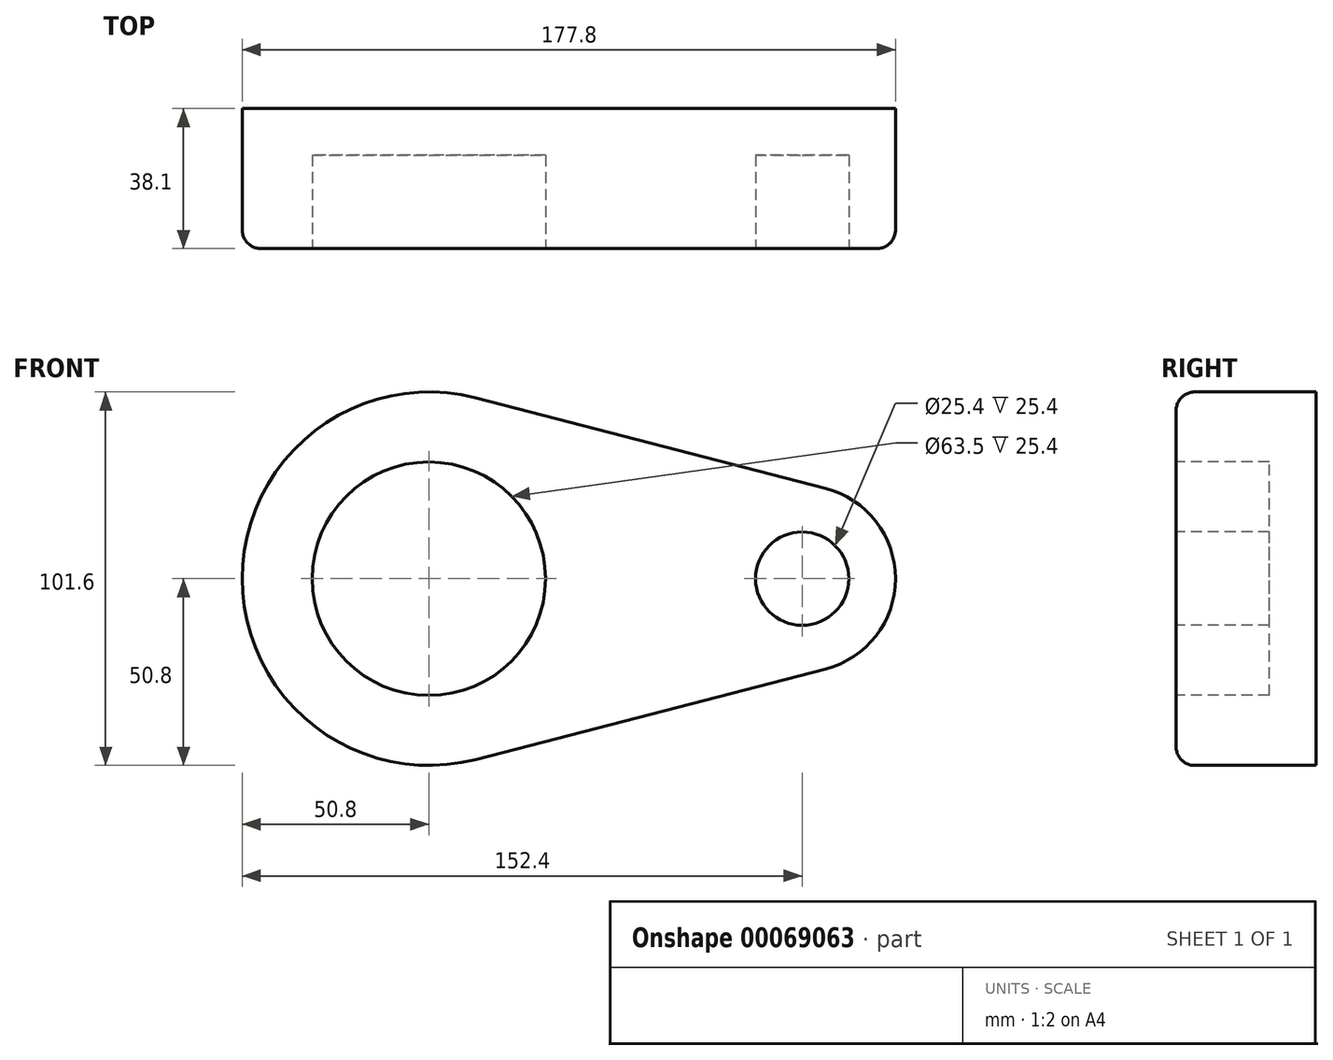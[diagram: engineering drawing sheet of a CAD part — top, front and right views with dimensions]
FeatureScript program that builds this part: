
annotation { "Feature Type Name" : "Feature", "Feature Type Description" : "" }
export const myFeature = defineFeature(function(context is Context, id is Id, definition is map)
    precondition{}
    {
        {
            var Q0;
            Q0=qCreatedBy(makeId("Front.planeOp"),FACE);
            var sketch = newSketch(context, id + "F3", { "sketchPlane" : qUnion([Q0])});
            skCircle(sketch, "E0", {"center": v(0, 0) * mm, "radius": 50.8 * mm});
            skCircle(sketch, "E1", {"center": v(101.6, 0) * mm, "radius": 25.4 * mm});
            skLineSegment(sketch, "E2", {"start": v(12.7, 49.19) * mm, "end": v(107.95, 24.6) * mm});
            skLineSegment(sketch, "E3", {"start": v(12.7, -49.19) * mm, "end": v(107.95, -24.6) * mm});
            skSolve(sketch);
        }
        {
            var Q0;
            {var subQ0=sQuery(id+"F3.wireOp",EDGE,"E2");Q0=makeQuery(id+"F3.imprint","IMPRINT",FACE,{"disambiguationData":[TD([[makeQuery(id+"F3.imprint","IMPRINT",EDGE,{"derivedFrom":subQ0}),-1.0]])]});}
            var Q1;
            {var subQ0=sQuery(id+"F3.wireOp",EDGE,"E0");var subQ1=makeQuery(id+"F3.imprint","INTERSECT",VERTEX,{"derivedFrom":[subQ0,sQuery(id+"F3.wireOp",EDGE,"E2")]});Q1=makeQuery(id+"F3.imprint","IMPRINT",FACE,{"disambiguationData":[TD([[makeQuery(id+"F3.imprint","IMPRINT",EDGE,{"disambiguationData":[TD([[subQ1,-1.0]])],"derivedFrom":subQ0}),1.0]])]});}
            var Q2;
            {var subQ0=sQuery(id+"F3.wireOp",EDGE,"E1");var subQ1=makeQuery(id+"F3.imprint","INTERSECT",VERTEX,{"derivedFrom":[subQ0,sQuery(id+"F3.wireOp",EDGE,"E2")]});Q2=makeQuery(id+"F3.imprint","IMPRINT",FACE,{"disambiguationData":[TD([[makeQuery(id+"F3.imprint","IMPRINT",EDGE,{"disambiguationData":[TD([[subQ1,-1.0]])],"derivedFrom":subQ0}),1.0]])]});}
            var Q3;
            Q3=sQuery(id+"F3.wireOp",EDGE,"E1");
            extrude(context, id + "F0", {"entities" : qUnion([Q0, Q1, Q2]), "surfaceEntities" : qUnion([Q3]), "depth" : 38.1 * mm});
        }
        {
            var Q0;
            Q0=makeQuery(id+"F0.opExtrude","CAP_FACE",FACE,{"disambiguationData":[OSD([sQuery(id+"F3.wireOp",EDGE,"E0"),sQuery(id+"F3.wireOp",EDGE,"E1"),sQuery(id+"F3.wireOp",EDGE,"E2"),sQuery(id+"F3.wireOp",EDGE,"E3")])],"isStart":false});
            var sketch = newSketch(context, id + "F1", { "sketchPlane" : qUnion([Q0])});
            skCircle(sketch, "E4", {"center": v(0, 0) * mm, "radius": 31.75 * mm});
            skCircle(sketch, "E5", {"center": v(101.6, 0) * mm, "radius": 12.7 * mm});
            skSolve(sketch);
        }
        {
            var Q0;
            Q0 = qSketchRegion(id + "F1", true);
            extrude(context, id + "F4", {"entities" : qUnion([Q0]), "operationType" : NewBodyOperationType.REMOVE, "oppositeDirection" : true, "depth" : 25.4 * mm});
        }
        {
            var Q0;
            Q0=makeQuery(id+"F4.boolean.opBoolean","COPY",EDGE,{"derivedFrom":makeQuery(id+"F4.opExtrude","CAP_EDGE",EDGE,{"disambiguationData":[OSD([sQuery(id+"F1.wireOp",EDGE,"E4")])],"isStart":true})});
            var Q1;
            Q1=makeQuery(id+"F4.boolean.opBoolean","COPY",EDGE,{"derivedFrom":makeQuery(id+"F4.opExtrude","CAP_EDGE",EDGE,{"disambiguationData":[OSD([sQuery(id+"F1.wireOp",EDGE,"E5")])],"isStart":true})});
            var Q2;
            Q2=makeQuery(id+"F0.opExtrude","CAP_EDGE",EDGE,{"disambiguationData":[OSD([sQuery(id+"F3.wireOp",EDGE,"E2")])],"isStart":false});
            fillet(context, id + "F2", {"entities" : qUnion([Q0, Q1, Q2]), "radius" : 5.08 * mm, "tangentPropagation" : true, "allowEdgeOverflow" : false});
        }
    });
